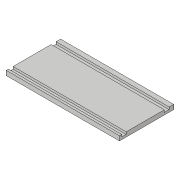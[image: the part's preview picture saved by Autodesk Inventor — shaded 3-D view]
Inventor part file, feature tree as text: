
AUTODESK INVENTOR PART (.ipt)
format: ipt  version: 2018.3 (Build 223284000, 284)  size: 92,672 bytes
history: native  units: in
note: dims shown in document units (in); Inventor stores cm internally (conversion verified against a paired STEP export)
features: extrude x2, sketch x2
ambient origin geometry x8: Origin, YZ Plane, XZ Plane, XY Plane, X Axis, Y Axis, Z Axis, Center Point
bodies: Solid1 (feature_tree)
feature tree (4):
  extrude  "Extrusion1"  Depth=0.125in TaperAngle=0.0deg
  extrude  "Extrusion2"  Depth=0.125in
  sketch  "Sketch1"  dims[d0=3.125in d1=1.5in d2=0.125in d3=0.0in]
  sketch  "Sketch2"  dims[d4=0.135in d5=0.125in d6=0.126in d7=0.0625in d8=0.0625in d9=0.0in]
